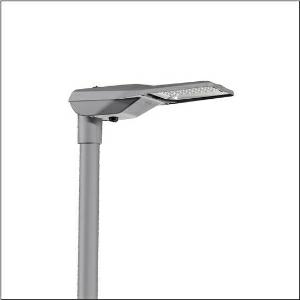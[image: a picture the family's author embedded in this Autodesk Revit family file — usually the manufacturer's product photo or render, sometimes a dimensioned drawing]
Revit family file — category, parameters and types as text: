
# Revit family: streetlight_sl_21_iq_mini___st1_0a_5xe2d31y08hb_7569
name_source: partatom
category: Lighting Fixtures
units: mm (PartAtom-declared; Revit-internal decimal feet)

## family parameters
Cut with Voids When Loaded = No
Host = Face
Light Source = No
Part Type = Normal
Room Calculation Point = No
Round Connector Dimension = Use Diameter
Shared = No

## types (1)
- --- (1 x LED, 9750 lm, 71 W, 3000K)
    Apparent Load = 71 VA
    CIE Flux Codes = 37 72 97 100 100
    Color Rendering = 70
    Color Temperature = 3000K
    Default Elevation = 1800 mm
    Description = Streetlight SL 21 iQ mini, mast luminaire, primary light control with lens, of PMMA, primary optical cover: cover, of toughened safety glass, transparent, light distribution: ST1.0a, light emission: direct distribution, primary light characteristic: asymmetric, installation type: post-top, side-entry, LED, High Power LED, rated luminous flux: 9.750lm, luminous efficacy: 137lm/W, light colour: 730, colour temperature: 3000K, control gear: iQ-Street Remote, D4i with power reduction, control: pre-setting: logarithmic dimming characteristic, Street-Remote, Auto-Match, Temp-Guard, Lumen-Switch, Night-Set, Smart-Wire, Light-Fading, Desk-Remote (wireless, voltage-free reading and setting of iQ features in the workshop via application-optimized NFC function/RFID function), optimised constant luminous flux control (CLO 2.0), mains connection: 220..240V, AC, 50/60Hz, start of lifetime: 71W, end of service life: 75W, reduction: 30W, luminaire housing, of diecast aluminium, powder-coated, SITECO metallic grey (DB 702S), corrosivity category C5 high according to DIN EN ISO 12944, please order mast flange separately, inclination adjustable: 0°, 5°, 10°, 15°, sealing non-destructively replaceable, multi-level sealing system, length: 628mm, width: 235mm, height: 110mm, mast flange for spigot size: 42mm (side-entry): 5XC10008XM4, 60/48mm (side-entry/post-top): 5XC10108XM2, 76/60mm (side-entry/post-top): 5XC10108XM1, mounting height: 4..8m, Smart Interface below and above, protection rating (complete): IP66, insulation class (complete): insulation class II (safety insulation), certification: CE, ENEC, ENEC+, VDE, impact resistance: IK10, permissible operating ambient temperature for outdoor applications: -40..+50°C, standard-compliant lighting for roads and squares, packaging unit: 1 piece

Light Distribution: ST1.0a
    Height = 110 mm
    Lamp = 1 x LED
    Lamp Light Flux = 9750 lm
    Lamp Power = 71 W
    Lamp count = 1
    Length = 625 mm
    Luminous efficacy = 137 lm/W
    Manufacturer = Siteco
    ModVariant = No
    Model = 5XE2D31Y08HB
    Number of Poles = 1
    OnlyDefault = Yes
    Power Factor = 1
    Product Name = Streetlight SL 21 iQ mini | ST1.0a
    Product group = mast luminaire | pylon top
    ProductGroupID = 6100
    Protection Class = Protection class II
    Protection Degree = IP 66
    RLX_Detail_Level = 1
    RLX_Emergency_Light_Flux = 0 lm
    RLX_Emergency_Type = 0
    RLX_Emergency_Type_DB = No
    RlxData = <blob elided: 92517 chars, md5=7b22d860>
    Socket = socket
    Standby Power = 0 W
    System Light Flux = 9750 lm
    System Power = 71 W
    Type Comments = factory setting: luminous flux: 100 % | dim-lin: 254 | 716 mA
    Type Image = l_1003514.jpg
    URL = http://relux.com
    VarID = @adj_114999
    Voltage = 0 V
    Weight = 0.00 kg
    Width = 234 mm

## geometry (parser evidence)
native form markers: Blend x4, Sweep x11
no freeform markers — native parametric forms only
